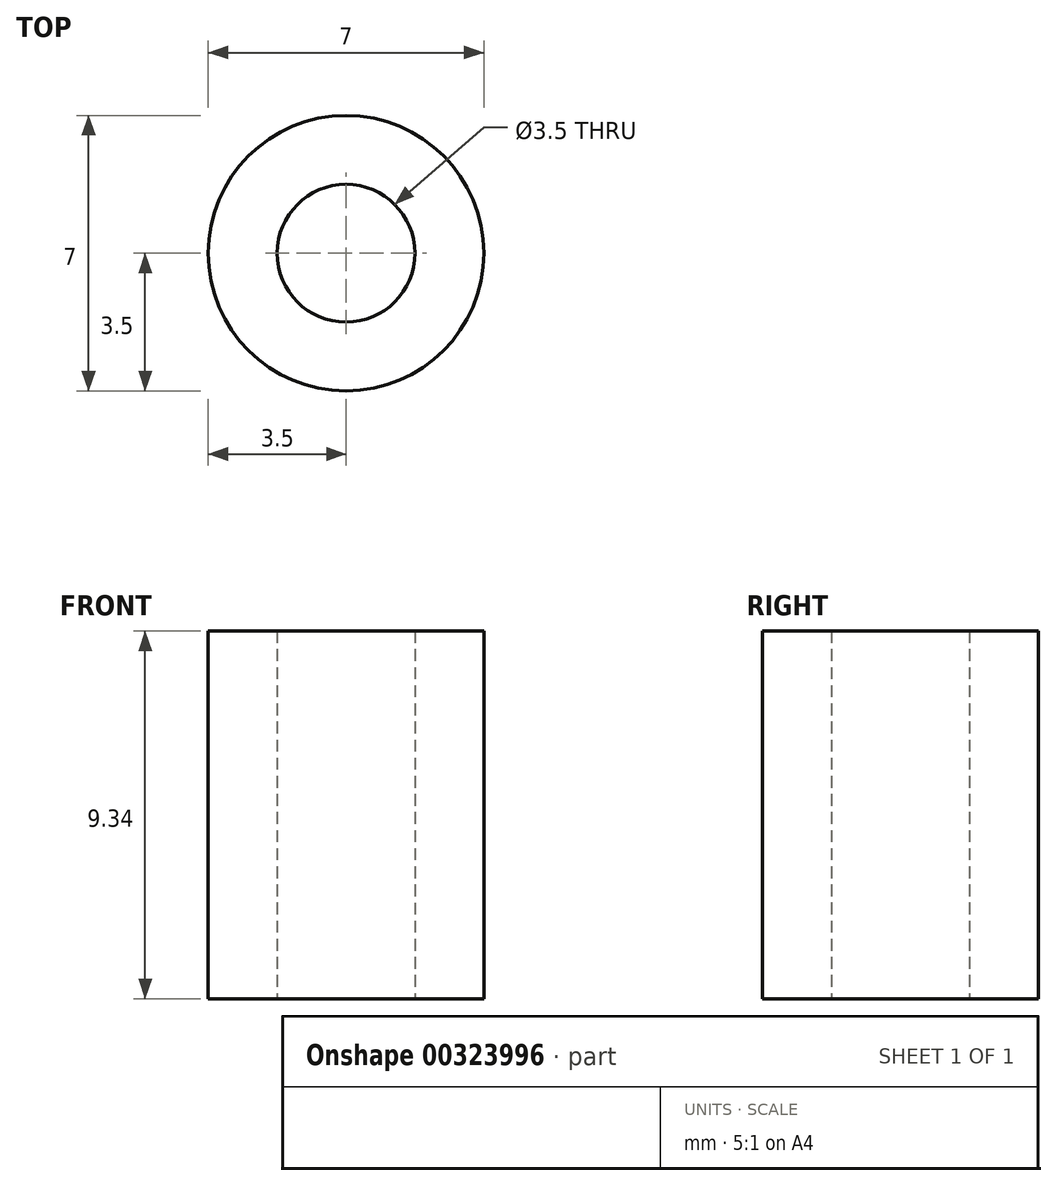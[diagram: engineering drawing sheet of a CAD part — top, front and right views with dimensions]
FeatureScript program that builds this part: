
annotation { "Feature Type Name" : "Feature", "Feature Type Description" : "" }
export const myFeature = defineFeature(function(context is Context, id is Id, definition is map)
    precondition{}
    {
        {
            var Q0;
            Q0=qCreatedBy(makeId("Top.planeOp"),FACE);
            var sketch = newSketch(context, id + "F0", { "sketchPlane" : qUnion([Q0])});
            skCircle(sketch, "E0", {"center": v(0, 0) * mm, "radius": 3.5 * mm});
            skCircle(sketch, "E1", {"center": v(0, 0) * mm, "radius": 1.75 * mm});
            skSolve(sketch);
        }
        {
            var Q0;
            Q0=makeQuery(id+"F0.imprint","IMPRINT",FACE,{"disambiguationData":[TD([[makeQuery(id+"F0.imprint","IMPRINT",EDGE,{"derivedFrom":sQuery(id+"F0.wireOp",EDGE,"E0")}),1.0]])]});
            extrude(context, id + "F1", {"entities" : qUnion([Q0]), "depth" : 9.34 * mm});
        }
    });
